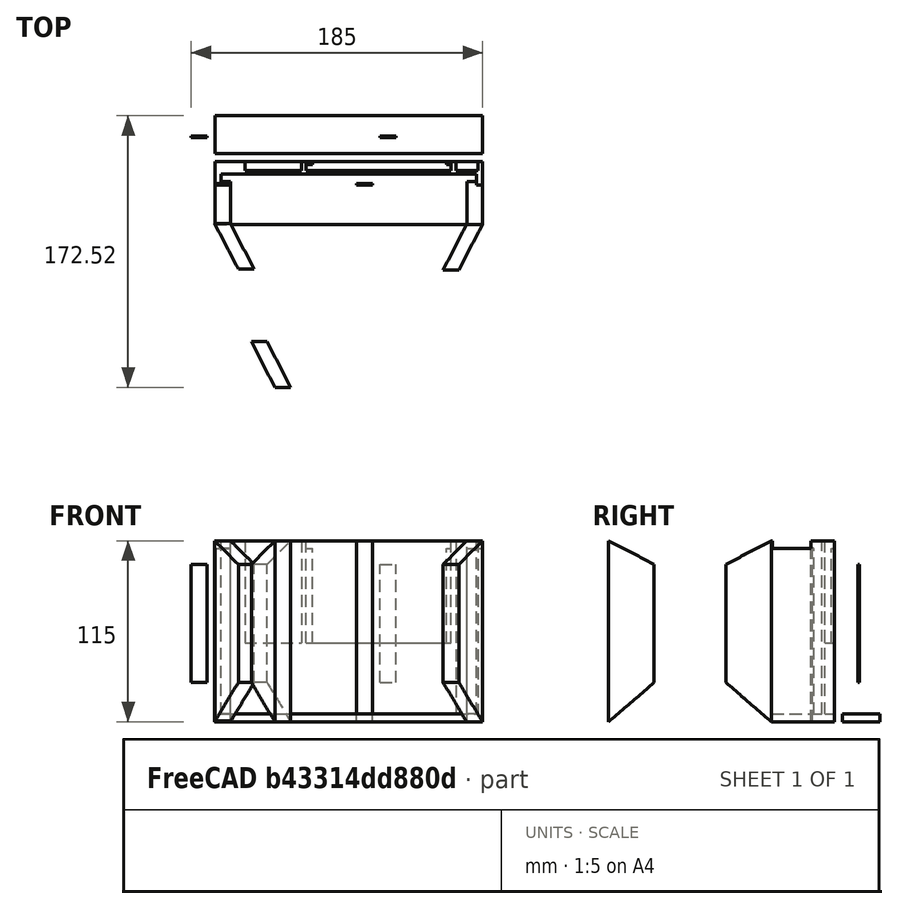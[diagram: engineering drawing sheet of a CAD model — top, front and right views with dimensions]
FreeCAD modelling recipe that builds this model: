
FCSTD DOCUMENT  (FreeCAD 0.15R4671 (Git))
Label: FINALHMD
License: All rights reserved
LicenseURL: http://en.wikipedia.org/wiki/All_rights_reserved
objects: Part::Box×17, Part::MultiFuse×5, Part::Cut×4, Part::Extrusion×3, Part::RuledSurface×2, App::DocumentObjectGroup×1
note: 31 computed .brp shape members not serialized (recipe doc carries the construction recipe); baked Part::Feature solids carry a one-line shape summary decoded from their .brp

FEATURE [Part::Box] Box  label="Cube"
  Height = 115
  Length = 170
  Width = 15
FEATURE [Part::Box] Box001  label="Cube001"
  Height = 110
  Length = 162
  Placement = pos=(4,0,5) rot=(0,0,1;0rad)
  Width = 7
FEATURE [Part::Box] Box002  label="Cube002"
  Height = 65
  Length = 92
  Placement = pos=(58,9,50) rot=(0,0,1;0rad)
  Width = 6
FEATURE [Part::Cut] Cut
  Base = -> Box
  Tool = -> Box001
FEATURE [Part::Cut] Cut001
  Base = -> Cut
  Tool = -> Box002
FEATURE [Part::Box] Box003  label="Cube003"
  Height = 110
  Length = 10
  Width = 2
FEATURE [Part::Box] Box004  label="Del"
  Height = 65
  Length = 36
  Placement = pos=(19,9,50) rot=(0,0,1;0rad)
  Width = 7
FEATURE [Part::Box] Box005  label="Cube005"
  Height = 110
  Length = 10
  Placement = pos=(160,0,0) rot=(0,0,1;0rad)
  Width = 2
FEATURE [Part::MultiFuse] Fusion
  Shapes = -> [Cut001,Box003,Box005]
FEATURE [Part::Box] Box006  label="Cube006"
  Height = 60
  Length = 4
  Placement = pos=(58,13,50) rot=(0,0,1;0rad)
  Width = 2
FEATURE [Part::Box] Box007  label="Cube007"
  Height = 60
  Length = 3
  Placement = pos=(147,13,50) rot=(0,0,1;0rad)
  Width = 2
FEATURE [Part::MultiFuse] Fusion001
  Shapes = -> [Fusion,Box006,Box007]
FEATURE [Part::Box] Box008  label="Cube008"
  Height = 110
  Length = 14
  Placement = pos=(153,9,5) rot=(0,0,1;0rad)
  Width = 7
FEATURE [Part::Cut] Cut002
  Base = -> Fusion001
  Tool = -> Box004
FEATURE [Part::Cut] Cut003
  Base = -> Cut002
  Tool = -> Box008
FEATURE [Part::Box] Box009  label="Cube009"
  Height = 110
  Length = 10
  Placement = pos=(0,-25,0) rot=(0,0,1;0rad)
  Width = 25
FEATURE [Part::Box] Box010  label="Cube010"
  Height = 110
  Length = 10
  Placement = pos=(160,-25,0) rot=(0,0,1;0rad)
  Width = 25
FEATURE [Part::Box] Box011  label="Cube011"
  Height = 5
  Length = 150
  Placement = pos=(10,-25,0) rot=(0,0,1;0rad)
  Width = 25
FEATURE [Part::MultiFuse] Fusion002
  Shapes = -> [Box009,Box010,Box011]
FEATURE [Part::MultiFuse] Fusion003
  Shapes = -> [Cut003,Fusion002]
FEATURE [Part::Box] Box012  label="Cube012"
  Height = 115
  Length = 10
  Width = 1
FEATURE [Part::Box] Box013  label="Cube013"
  Height = 75
  Length = 10
  Placement = pos=(-15,30,25) rot=(0,0,1;0rad)
  Width = 1
FEATURE [Part::RuledSurface] Ruled_Surface
  Curve1 = -> Box013 [Edge5]
  Curve2 = -> Box012 [Edge7]
  Orientation = 0
  Placement = pos=(38.1258,-129.525,0.00145359) rot=(0,0,1;0rad)
FEATURE [Part::Extrusion] Extrude
  Base = -> Ruled_Surface
  Dir = (-10,0,0)
  Placement = pos=(48,-153,0) rot=(0,0,1;3.14159rad)
  Solid = false
FEATURE [Part::Extrusion] Extrude001
  Base = -> Ruled_Surface
  Dir = (-10,0,0)
  Solid = false
FEATURE [Part::Box] Box014  label="Cube014"
  Height = 115
  Length = 10
  Placement = pos=(90,0,0) rot=(0,0,1;0rad)
  Width = 1
FEATURE [Part::Box] Box015  label="Cube004"
  Height = 75
  Length = 10
  Placement = pos=(105,30,25) rot=(0,0,1;0rad)
  Width = 1
FEATURE [Part::RuledSurface] Ruled_Surface001
  Curve1 = -> Box014 [Edge7]
  Curve2 = -> Box015 [Edge5]
  Orientation = 0
  Placement = pos=(-6.95853,-117.976,0.000840802) rot=(0,0,1;0rad)
FEATURE [Part::Extrusion] Extrude002
  Base = -> Ruled_Surface001
  Dir = (-10,0,0)
  Placement = pos=(253,-142,0) rot=(0,0,1;3.14159rad)
  Solid = false
FEATURE [Part::Box] Box016  label="Cube015"
  Height = 5
  Length = 170
  Placement = pos=(0,20,0) rot=(0,0,1;0rad)
  Width = 24
FEATURE [Part::MultiFuse] Fusion004
  Shapes = -> [Extrude002,Box016,Extrude,Fusion003]
FEATURE [App::DocumentObjectGroup] Group
  Group = -> [Ruled_Surface,Ruled_Surface001,Fusion004]
